# Revit family: Dunbar 100 ETL
name_source: partatom
category: Lighting Fixtures
revit_build: Autodesk Revit 2018 (Build: 20170223_1515(x64)
units: mm (PartAtom-declared; Revit-internal decimal feet)

## family parameters
Always vertical = Yes
Cut with Voids When Loaded = No
Host = Wall
Light Source = Yes
OmniClass Number = 23.80.70.00
OmniClass Title = Lighting
Part Type = Normal
Room Calculation Point = No
Round Connector Dimension = Use Diameter
Shared = No

## types (3) — shared parameters
ADA compliant = NO
Color Filter = 16777215
Dimmable = No
Dimming Lamp Color Temperature Shift = <None>
Driver Included = Yes
Driver Required = No
Efficacy (lm/w) = 17
Electrical Class = 1
Emit from Line Length = 610 mm
Lamp = LED
Length of Cable Supplied = 150 mm
Light Source Fixed = Yes
Location rating = WET
Main Material = Metal - Aluminium
Manufacturer = Astro Lighting Ltd
Photometric Web File = GNC-21601 Dunbar 100 [ETL] Texture Black inc sphere.ies
Power (Watts) = 3.1
Product Location = Outdoor
Tilt Angle = 90.00°
URL = www.astrolighting.com

## per-type parameters (varying)
| type | Main Finish | Product Code | Product Name | Product SKU |
| Dunbar 100 Textured White | Textured White | 7493 | Dunbar 100 Textured White | 1298005 |
| Dunbar 100 Textured Black | Textured Black | 7109 | Dunbar 100 Textured Black | 1298004 |
| Dunbar100 Textured Grey | Textured Grey | 8194 | Dunbar 100 Textured Grey | 1298022 |

## geometry (parser evidence)
native form markers: Sweep x3
no freeform markers — native parametric forms only
